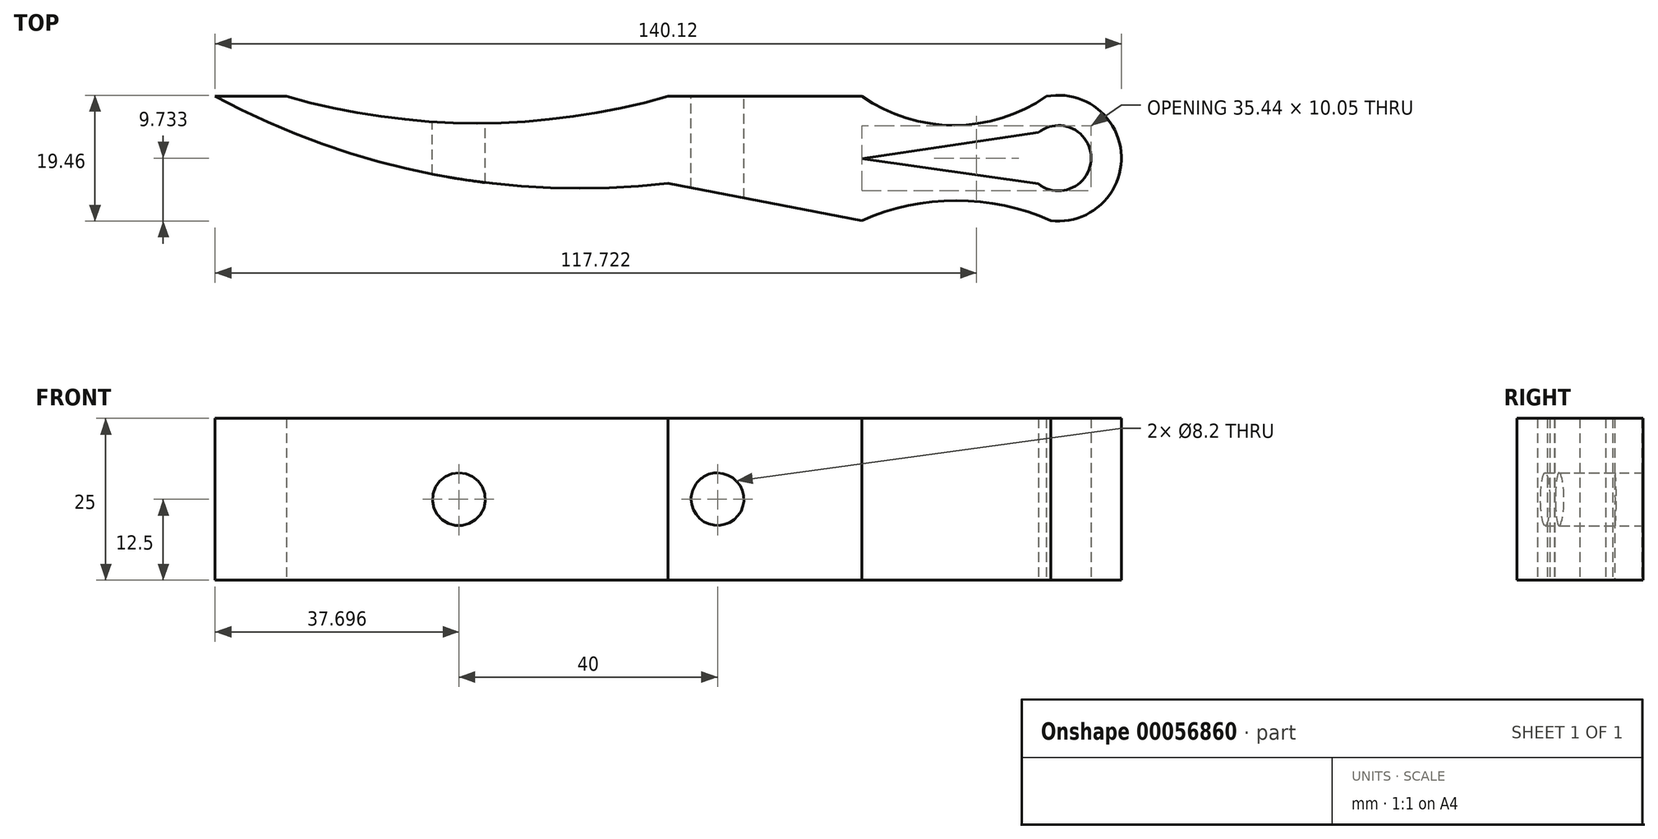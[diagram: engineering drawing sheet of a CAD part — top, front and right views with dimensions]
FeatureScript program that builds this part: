
annotation { "Feature Type Name" : "Feature", "Feature Type Description" : "" }
export const myFeature = defineFeature(function(context is Context, id is Id, definition is map)
    precondition{}
    {
        {
            var Q0;
            Q0=qCreatedBy(makeId("Top.planeOp"),FACE);
            var sketch = newSketch(context, id + "F0", { "sketchPlane" : qUnion([Q0])});
            skLineSegment(sketch, "E0", {"start": v(46.05, 0) * mm, "end": v(-44.42, 0) * mm, "construction": true});
            skLineSegment(sketch, "E1", {"start": v(0, 13.34) * mm, "end": v(0, -19.2) * mm, "construction": true});
            skLineSegment(sketch, "E2.0", {"start": v(-70, 13.34) * mm, "end": v(-70, -19.2) * mm, "construction": true});
            skLineSegment(sketch, "E3.0", {"start": v(70, 0) * mm, "end": v(70, -19.2) * mm, "construction": true});
            skLineSegment(sketch, "E4.0", {"start": v(30, 0) * mm, "end": v(30, -19.2) * mm, "construction": true});
            skLineSegment(sketch, "E5", {"start": v(0, -13.44) * mm, "end": v(30, -19.2) * mm});
            skLineSegment(sketch, "E6", {"start": v(30, 0) * mm, "end": v(0, 0) * mm});
            skLineSegment(sketch, "E7", {"start": v(70, 0) * mm, "end": v(61.94, 0) * mm, "construction": true});
            skArc(sketch, "E8", {"start": v(59.18, -19.2) * mm, "mid": v(70.11, -9.22) * mm, "end": v(58.53, 0) * mm});
            skArc(sketch, "E9", {"start": v(30, 0) * mm, "mid": v(44.26, -4.46) * mm, "end": v(58.53, 0) * mm});
            skArc(sketch, "E10", {"start": v(59.18, -19.2) * mm, "mid": v(44.59, -16.1) * mm, "end": v(30, -19.2) * mm});
            skLineSegment(sketch, "E11", {"start": v(-70, 0) * mm, "end": v(-58.96, 0) * mm});
            skArc(sketch, "E12", {"start": v(-70, 0) * mm, "mid": v(-36.03, -12.1) * mm, "end": v(0, -13.44) * mm});
            skArc(sketch, "E13", {"start": v(-58.96, 0) * mm, "mid": v(-29.48, -4.15) * mm, "end": v(0, 0) * mm});
            skCircle(sketch, "E14", {"center": v(60.4, -9.55) * mm, "radius": 5.05 * mm});
            skLineSegment(sketch, "E15", {"start": v(30, -9.6) * mm, "end": v(57.28, -5.57) * mm});
            skLineSegment(sketch, "E16", {"start": v(30, -9.6) * mm, "end": v(57.28, -13.53) * mm});
            skSolve(sketch);
        }
        {
            var Q0;
            Q0=makeQuery(id+"F0.imprint","IMPRINT",FACE,{"disambiguationData":[TD([[makeQuery(id+"F0.imprint","IMPRINT",EDGE,{"derivedFrom":sQuery(id+"F0.wireOp",EDGE,"E5")}),1.0]])]});
            extrude(context, id + "F1", {"entities" : qUnion([Q0]), "depth" : 25 * mm});
        }
        {
            var Q0;
            Q0=makeQuery(id+"F1.opExtrude","SWEPT_FACE",FACE,{"disambiguationData":[OSD([sQuery(id+"F0.wireOp",EDGE,"E6")])]});
            var sketch = newSketch(context, id + "F2", { "sketchPlane" : qUnion([Q0])});
            skLineSegment(sketch, "E17", {"start": v(-30, 12.5) * mm, "end": v(0, 12.5) * mm, "construction": true});
            skCircle(sketch, "E18", {"center": v(-7.7, 12.5) * mm, "radius": 4.1 * mm});
            skCircle(sketch, "E19.MirrorC", {"center": v(7.7, 12.5) * mm, "radius": 4.1 * mm});
            skLineSegment(sketch, "E20.0", {"start": v(20, 5) * mm, "end": v(20, 0) * mm});
            skLineSegment(sketch, "E20.1", {"start": v(20, 5) * mm, "end": v(70, 5) * mm});
            skCircle(sketch, "E21.MirrorC", {"center": v(32.3, 12.5) * mm, "radius": 4.1 * mm});
            skCircle(sketch, "E22.MirrorC", {"center": v(47.7, 12.5) * mm, "radius": 4.1 * mm});
            skSolve(sketch);
        }
        {
            var Q0;
            Q0=makeQuery(id+"F2.imprint","IMPRINT",FACE,{"disambiguationData":[TD([[makeQuery(id+"F2.imprint","IMPRINT",EDGE,{"derivedFrom":sQuery(id+"F2.wireOp",EDGE,"E18")}),1.0]])]});
            var Q1;
            Q1=makeQuery(id+"F2.imprint","IMPRINT",FACE,{"disambiguationData":[TD([[makeQuery(id+"F2.imprint","IMPRINT",EDGE,{"derivedFrom":sQuery(id+"F2.wireOp",EDGE,"E19.MirrorC")}),-1.0]])]});
            var Q2;
            Q2=makeQuery(id+"F2.imprint","IMPRINT",FACE,{"disambiguationData":[TD([[makeQuery(id+"F2.imprint","IMPRINT",EDGE,{"derivedFrom":sQuery(id+"F2.wireOp",EDGE,"E21.MirrorC")}),1.0]])]});
            var Q3;
            Q3=makeQuery(id+"F2.imprint","IMPRINT",FACE,{"disambiguationData":[TD([[makeQuery(id+"F2.imprint","IMPRINT",EDGE,{"derivedFrom":sQuery(id+"F2.wireOp",EDGE,"E22.MirrorC")}),-1.0]])]});
            extrude(context, id + "F3", {"entities" : qUnion([Q0, Q1, Q2, Q3]), "operationType" : NewBodyOperationType.REMOVE, "oppositeDirection" : true, "depth" : 25 * mm});
        }
    });
